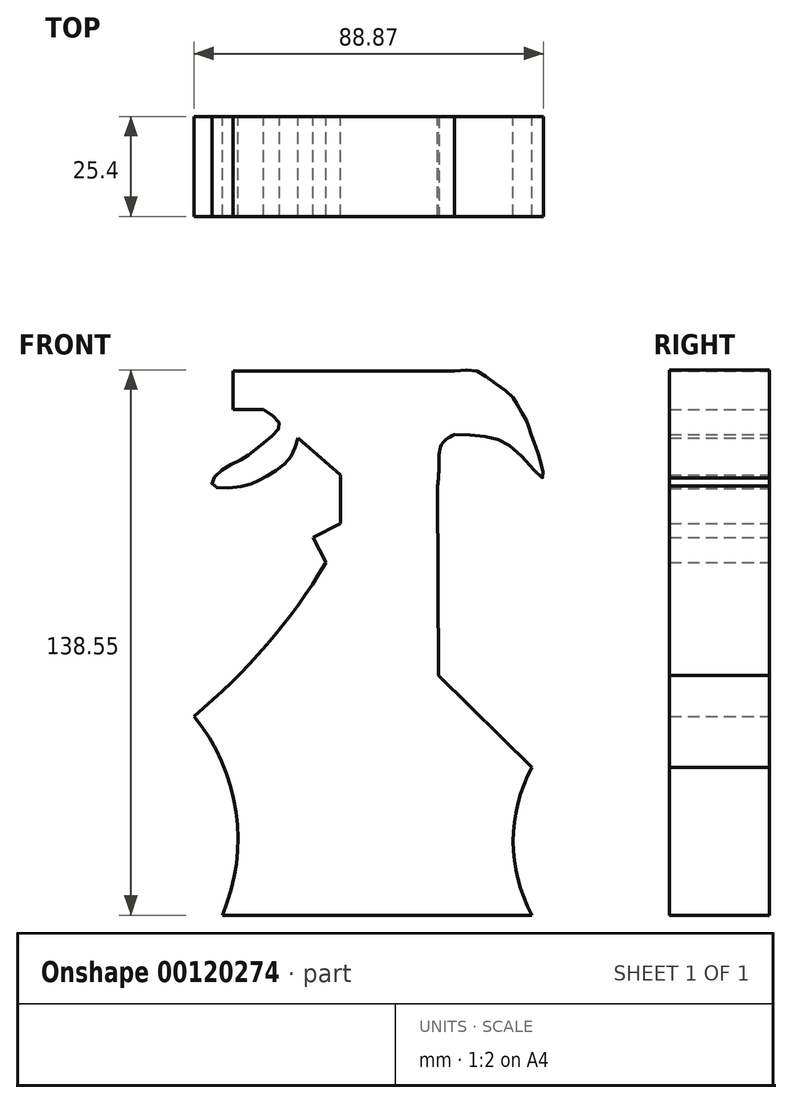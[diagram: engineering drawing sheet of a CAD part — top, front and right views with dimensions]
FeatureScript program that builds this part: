
annotation { "Feature Type Name" : "Feature", "Feature Type Description" : "" }
export const myFeature = defineFeature(function(context is Context, id is Id, definition is map)
    precondition{}
    {
        {
            var Q0;
            Q0=qCreatedBy(makeId("Front.planeOp"),FACE);
            var sketch = newSketch(context, id + "F0", { "sketchPlane" : qUnion([Q0])});
            skLineSegment(sketch, "E0", {"start": v(-33.67, 56.17) * mm, "end": v(-33.67, 46.34) * mm});
            skLineSegment(sketch, "E1", {"start": v(-33.67, 56.17) * mm, "end": v(22.65, 56.17) * mm});
            skFitSpline(sketch, "E2", {"points": [v(22.65, 56.17) * mm, v(28.2, 56.17) * mm, v(32.36, 53.44) * mm, v(37.13, 49.87) * mm, v(38.62, 47.48) * mm, v(40.71, 43.9) * mm, v(41.3, 42.72) * mm, v(42.5, 38.84) * mm, v(43.99, 34.97) * mm, v(44.29, 33.48) * mm, v(45.18, 29) * mm, v(39.22, 34.97) * mm, v(32.07, 39.14) * mm, v(22.65, 40.03) * mm], "startDerivative": vector(70.96, 8.83) * mm, "endDerivative": vector(-91.5, 3.32) * mm});
            skFitSpline(sketch, "E3", {"points": [v(22.65, 40.03) * mm, v(19.25, 37.34) * mm, v(18.65, 31.68) * mm, v(18.35, 26.91) * mm], "startDerivative": vector(-13.12, -6.7) * mm, "endDerivative": vector(-1.34, -13.7) * mm});
            skLineSegment(sketch, "E4", {"start": v(18.35, 26.91) * mm, "end": v(18.5, -21.25) * mm});
            skLineSegment(sketch, "E5", {"start": v(18.5, -21.25) * mm, "end": v(42.31, -44.55) * mm});
            skArc(sketch, "E6", {"start": v(42.31, -44.55) * mm, "mid": v(37.54, -63.33) * mm, "end": v(42.31, -82.1) * mm});
            skLineSegment(sketch, "E7", {"start": v(42.9, -82.1) * mm, "end": v(-36.34, -82.1) * mm});
            skArc(sketch, "E8", {"start": v(-36.34, -82.1) * mm, "mid": v(-32.9, -55.82) * mm, "end": v(-43.6, -31.57) * mm});
            skLineSegment(sketch, "E9", {"start": v(-33.67, 46.34) * mm, "end": v(-25.92, 46.34) * mm});
            skFitSpline(sketch, "E10", {"points": [v(-25.92, 46.34) * mm, v(-21.81, 42.3) * mm, v(-25.92, 37.88) * mm, v(-30.65, 34.1) * mm, v(-36.97, 30.62) * mm, v(-38.86, 27.15) * mm, v(-31.28, 26.83) * mm, v(-25.92, 29.04) * mm, v(-19.92, 33.15) * mm, v(-17.08, 39.15) * mm], "startDerivative": vector(58.3, -36.8) * mm, "endDerivative": vector(17.46, 56.18) * mm});
            skLineSegment(sketch, "E11", {"start": v(-6.34, 29.67) * mm, "end": v(-17.08, 39.15) * mm});
            skLineSegment(sketch, "E12", {"start": v(-6.34, 29.67) * mm, "end": v(-6.34, 17.36) * mm});
            skLineSegment(sketch, "E13", {"start": v(-6.34, 17.36) * mm, "end": v(-13.29, 13.89) * mm});
            skLineSegment(sketch, "E14", {"start": v(-13.29, 13.89) * mm, "end": v(-10.07, 7.45) * mm});
            skArc(sketch, "E15", {"start": v(-43.6, -31.57) * mm, "mid": v(-25.16, -13.5) * mm, "end": v(-10.07, 7.45) * mm});
            skSolve(sketch);
        }
        {
            var Q0;
            Q0 = qSketchRegion(id + "F0", true);
            var Q1;
            Q1=makeQuery(id+"F0.imprint","IMPRINT",FACE,{"disambiguationData":[TD([[makeQuery(id+"F0.imprint","IMPRINT",EDGE,{"derivedFrom":sQuery(id+"F0.wireOp",EDGE,"E0")}),1.0]])]});
            extrude(context, id + "F1", {"entities" : qUnion([Q0, Q1]), "depth" : 25.4 * mm});
        }
    });
